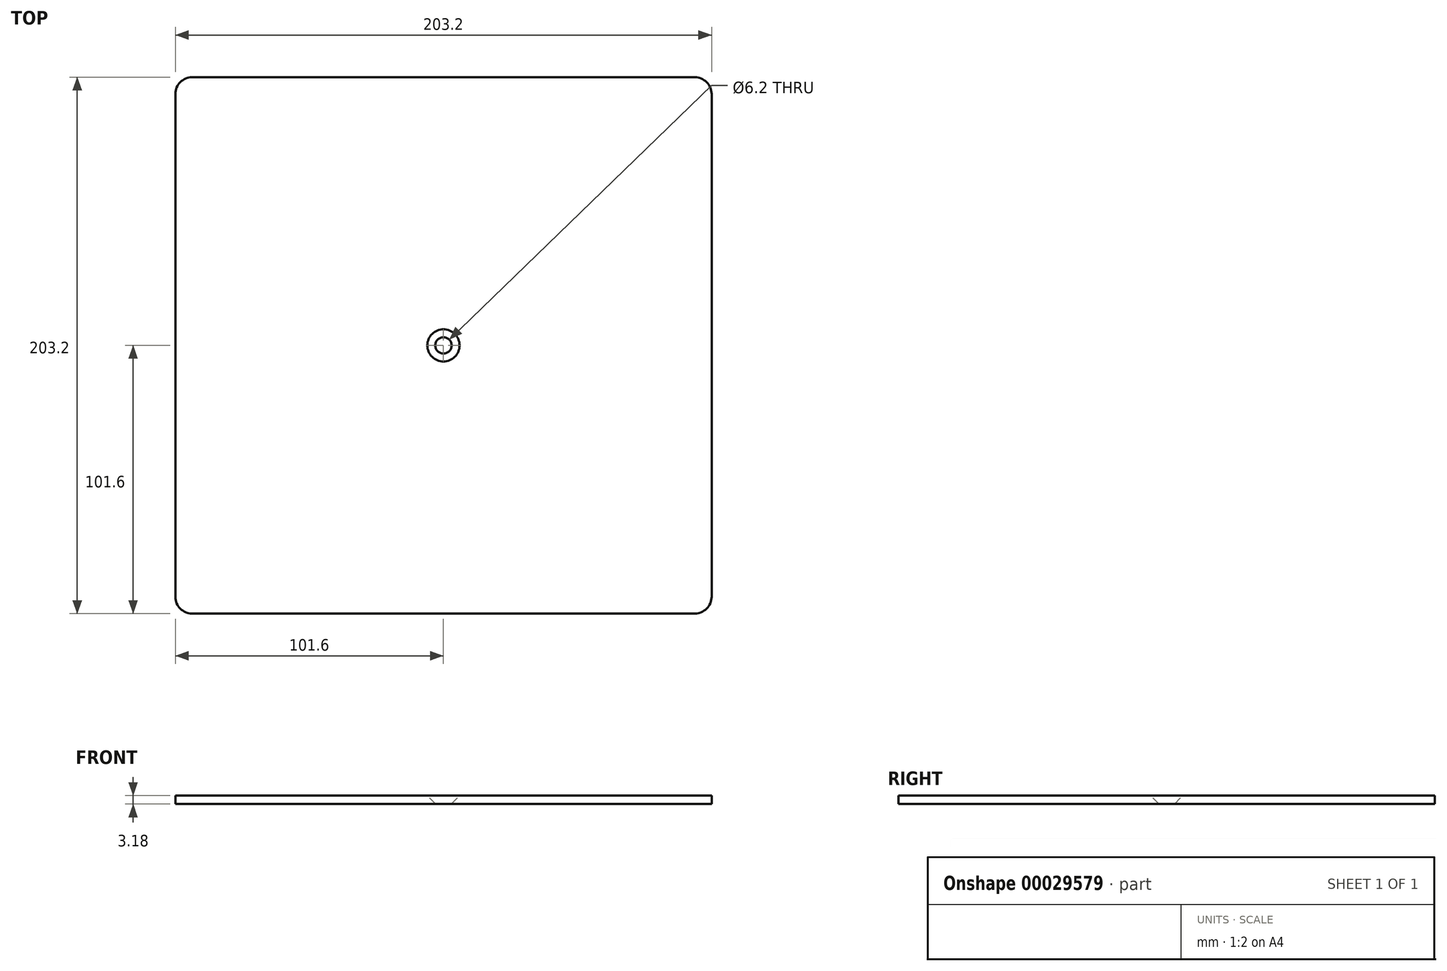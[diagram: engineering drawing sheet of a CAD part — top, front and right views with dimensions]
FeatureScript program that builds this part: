
annotation { "Feature Type Name" : "Feature", "Feature Type Description" : "" }
export const myFeature = defineFeature(function(context is Context, id is Id, definition is map)
    precondition{}
    {
        {
            var Q0;
            Q0=qCreatedBy(makeId("Top.planeOp"),FACE);
            var sketch = newSketch(context, id + "F0", { "sketchPlane" : qUnion([Q0])});
            skLineSegment(sketch, "E0.rect.bottom", {"start": v(-101.6, 101.6) * mm, "end": v(101.6, 101.6) * mm});
            skLineSegment(sketch, "E0.rect.top", {"start": v(-101.6, -101.6) * mm, "end": v(101.6, -101.6) * mm});
            skLineSegment(sketch, "E0.rect.left", {"start": v(-101.6, 101.6) * mm, "end": v(-101.6, -101.6) * mm});
            skLineSegment(sketch, "E0.rect.right", {"start": v(101.6, 101.6) * mm, "end": v(101.6, -101.6) * mm});
            skPoint(sketch, "E0.rect.middle", {"position": v(0, 0) * mm});
            skSolve(sketch);
        }
        {
            var Q0;
            Q0 = qSketchRegion(id + "F0", true);
            extrude(context, id + "F1", {"entities" : qUnion([Q0]), "depth" : 3.17 * mm});
        }
        {
            var Q0;
            Q0=makeQuery(id+"F1.opExtrude","SWEPT_EDGE",EDGE,{"disambiguationData":[OSD([sQuery(id+"F0.wireOp",EDGE,"E0.rect.top"),sQuery(id+"F0.wireOp",EDGE,"E0.rect.left")])]});
            var Q1;
            Q1=makeQuery(id+"F1.opExtrude","SWEPT_EDGE",EDGE,{"disambiguationData":[OSD([sQuery(id+"F0.wireOp",EDGE,"E0.rect.top"),sQuery(id+"F0.wireOp",EDGE,"E0.rect.right")])]});
            var Q2;
            Q2=makeQuery(id+"F1.opExtrude","SWEPT_EDGE",EDGE,{"disambiguationData":[OSD([sQuery(id+"F0.wireOp",EDGE,"E0.rect.bottom"),sQuery(id+"F0.wireOp",EDGE,"E0.rect.right")])]});
            var Q3;
            Q3=makeQuery(id+"F1.opExtrude","SWEPT_EDGE",EDGE,{"disambiguationData":[OSD([sQuery(id+"F0.wireOp",EDGE,"E0.rect.bottom"),sQuery(id+"F0.wireOp",EDGE,"E0.rect.left")])]});
            fillet(context, id + "F2", {"entities" : qUnion([Q0, Q1, Q2, Q3]), "radius" : 6.35 * mm, "allowEdgeOverflow" : false});
        }
        {
            var Q0;
            Q0=makeQuery(id+"F1.opExtrude","CAP_FACE",FACE,{"disambiguationData":[OSD([sQuery(id+"F0.wireOp",EDGE,"E0.rect.bottom"),sQuery(id+"F0.wireOp",EDGE,"E0.rect.top"),sQuery(id+"F0.wireOp",EDGE,"E0.rect.left"),sQuery(id+"F0.wireOp",EDGE,"E0.rect.right")])],"isStart":false});
            var sketch = newSketch(context, id + "F3", { "sketchPlane" : qUnion([Q0])});
            skPoint(sketch, "E1", {"position": v(0, 0) * mm});
            skSolve(sketch);
        }
        {
            var Q0;
            Q0=sQuery(id+"F3.wireOp",VERTEX,"E1");
            var Q1;
            Q1=makeQuery(id+"F1.opExtrude","SWEPT_BODY",BODY,{"disambiguationData":[OSD([sQuery(id+"F0.wireOp",EDGE,"E0.rect.bottom"),sQuery(id+"F0.wireOp",EDGE,"E0.rect.top"),sQuery(id+"F0.wireOp",EDGE,"E0.rect.left"),sQuery(id+"F0.wireOp",EDGE,"E0.rect.right")])]});
            hole(context, id + "F4", {"style" : HoleStyle.C_SINK, "holeDiameter" : 6.2 * mm, "cSinkDiameter" : 12.2 * mm, "endStyle" : HoleEndStyle.THROUGH, "locations" : qUnion([Q0]), "scope" : qUnion([Q1]), "cSinkAngle" : 90 * degree});
        }
    });
